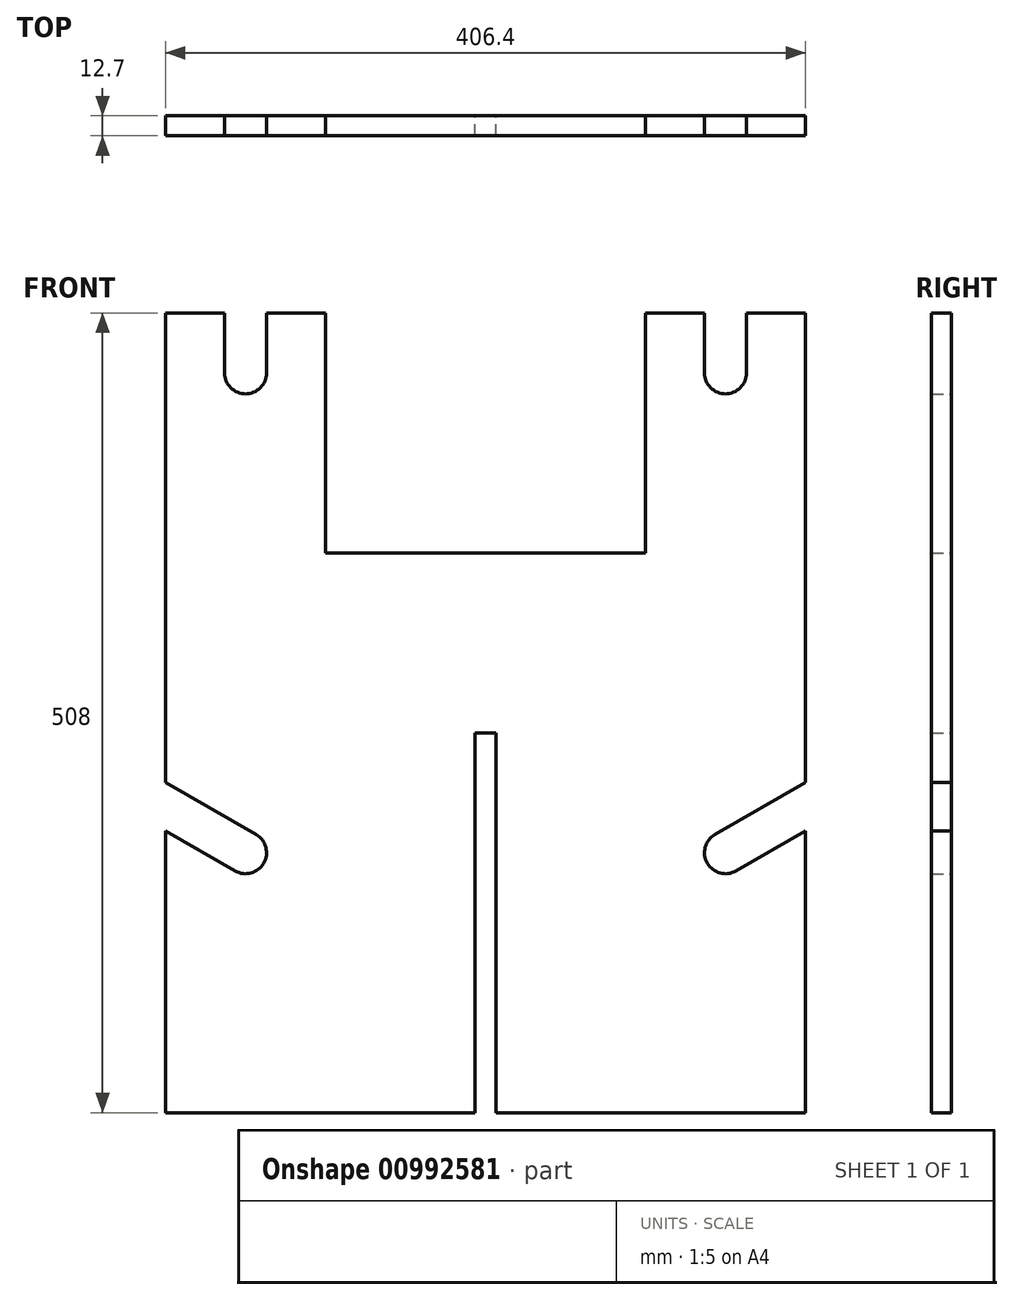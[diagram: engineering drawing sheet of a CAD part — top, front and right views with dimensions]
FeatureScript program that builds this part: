
annotation { "Feature Type Name" : "Feature", "Feature Type Description" : "" }
export const myFeature = defineFeature(function(context is Context, id is Id, definition is map)
    precondition{}
    {
        {
            var Q0;
            Q0=qCreatedBy(makeId("Front.planeOp"),FACE);
            var sketch = newSketch(context, id + "F0", { "sketchPlane" : qUnion([Q0])});
            skLineSegment(sketch, "E0.bottom", {"start": v(-203.2, 254) * mm, "end": v(-165.73, 254) * mm});
            skLineSegment(sketch, "E0.top", {"start": v(-203.2, -254) * mm, "end": v(-184.4, -254) * mm});
            skLineSegment(sketch, "E0.left", {"start": v(-203.2, 254) * mm, "end": v(-203.2, -254) * mm});
            skLineSegment(sketch, "E0.right", {"start": v(203.2, 254) * mm, "end": v(203.2, -254) * mm});
            skPoint(sketch, "E0.middle", {"position": v(0, 0) * mm});
            skPoint(sketch, "E1", {"position": v(-101.6, 254) * mm});
            skLineSegment(sketch, "E2", {"start": v(0, 0) * mm, "end": v(0, 371.22) * mm, "construction": true});
            skLineSegment(sketch, "E3", {"start": v(0, 0) * mm, "end": v(0, -352.5) * mm, "construction": true});
            skLineSegment(sketch, "E4", {"start": v(-249.7, -12.7) * mm, "end": v(258.3, -12.7) * mm, "construction": true});
            skLineSegment(sketch, "E5", {"start": v(-101.6, 254) * mm, "end": v(-101.6, 101.6) * mm});
            skLineSegment(sketch, "E6", {"start": v(-101.6, 101.6) * mm, "end": v(0, 101.6) * mm});
            skPoint(sketch, "E7", {"position": v(-177.8, -12.7) * mm});
            skPoint(sketch, "E8", {"position": v(-184.4, -12.7) * mm});
            skPoint(sketch, "E9.MirrorP", {"position": v(-171.2, -12.7) * mm});
            skLineSegment(sketch, "E10", {"start": v(-184.4, -12.7) * mm, "end": v(-171.2, -12.7) * mm});
            skLineSegment(sketch, "E11.trimOffspring", {"start": v(-171.2, -254) * mm, "end": v(-6.6, -254) * mm});
            skLineSegment(sketch, "E12.MirrorCS", {"start": v(101.6, 254) * mm, "end": v(101.6, 101.6) * mm});
            skLineSegment(sketch, "E13.MirrorCS", {"start": v(101.6, 101.6) * mm, "end": v(0, 101.6) * mm});
            skLineSegment(sketch, "E14.trimOffspring", {"start": v(101.6, 254) * mm, "end": v(203.2, 254) * mm});
            skLineSegment(sketch, "E15", {"start": v(171.2, -12.7) * mm, "end": v(184.4, -12.7) * mm});
            skLineSegment(sketch, "E16.trimOffspring", {"start": v(184.4, -254) * mm, "end": v(203.2, -254) * mm});
            skLineSegment(sketch, "E17", {"start": v(-184.4, -254) * mm, "end": v(-170.47, -254) * mm});
            skLineSegment(sketch, "E18", {"start": v(171.2, -254) * mm, "end": v(188.53, -254) * mm});
            skPoint(sketch, "E19", {"position": v(-6.6, -254) * mm});
            skPoint(sketch, "E20.MirrorP", {"position": v(6.6, -254) * mm});
            skLineSegment(sketch, "E21", {"start": v(-6.6, -254) * mm, "end": v(-6.6, -12.7) * mm});
            skLineSegment(sketch, "E22", {"start": v(-6.6, -12.7) * mm, "end": v(6.6, -12.7) * mm});
            skLineSegment(sketch, "E23", {"start": v(6.6, -12.7) * mm, "end": v(6.6, -254) * mm});
            skLineSegment(sketch, "E24.trimOffspring", {"start": v(6.6, -254) * mm, "end": v(171.2, -254) * mm});
            skPoint(sketch, "E25", {"position": v(-152.4, 254) * mm});
            skPoint(sketch, "E26.MirrorP", {"position": v(152.4, 254) * mm});
            skArc(sketch, "E27", {"start": v(-165.73, 215.9) * mm, "mid": v(-152.4, 202.57) * mm, "end": v(-139.06, 215.9) * mm});
            skLineSegment(sketch, "E28", {"start": v(-165.73, 215.9) * mm, "end": v(-165.73, 254) * mm});
            skLineSegment(sketch, "E29", {"start": v(-139.06, 215.9) * mm, "end": v(-139.06, 254) * mm});
            skLineSegment(sketch, "E30.trimOffspring", {"start": v(-139.06, 254) * mm, "end": v(-101.6, 254) * mm});
            skLineSegment(sketch, "E31.MirrorCS", {"start": v(165.73, 215.9) * mm, "end": v(165.73, 254) * mm});
            skArc(sketch, "E32.MirrorCS", {"start": v(165.73, 215.9) * mm, "mid": v(152.4, 202.57) * mm, "end": v(139.06, 215.9) * mm});
            skLineSegment(sketch, "E33.MirrorCS", {"start": v(139.06, 215.9) * mm, "end": v(139.06, 254) * mm});
            skLineSegment(sketch, "E34", {"start": v(-152.4, 215.9) * mm, "end": v(-152.4, -73.5) * mm, "construction": true});
            skLineSegment(sketch, "E35.MirrorCS", {"start": v(152.4, 215.9) * mm, "end": v(152.4, -73.5) * mm, "construction": true});
            skArc(sketch, "E36", {"start": v(-159.07, -100.45) * mm, "mid": v(-140.85, -95.57) * mm, "end": v(-145.73, -77.35) * mm});
            skArc(sketch, "E37.MirrorC", {"start": v(159.07, -100.45) * mm, "mid": v(140.85, -95.57) * mm, "end": v(145.73, -77.35) * mm});
            skLineSegment(sketch, "E38", {"start": v(-159.07, -100.45) * mm, "end": v(-203.2, -74.97) * mm});
            skLineSegment(sketch, "E39", {"start": v(-145.73, -77.35) * mm, "end": v(-203.2, -44.17) * mm});
            skLineSegment(sketch, "E40.MirrorCS", {"start": v(145.73, -77.35) * mm, "end": v(203.2, -44.17) * mm});
            skLineSegment(sketch, "E41.MirrorCS", {"start": v(159.07, -100.45) * mm, "end": v(203.2, -74.97) * mm});
            skSolve(sketch);
        }
        {
            var Q0;
            Q0=makeQuery(id+"F0.imprint","IMPRINT",FACE,{"disambiguationData":[TD([[makeQuery(id+"F0.imprint","IMPRINT",EDGE,{"derivedFrom":sQuery(id+"F0.wireOp",EDGE,"E0.bottom")}),-1.0]])]});
            extrude(context, id + "F1", {"entities" : qUnion([Q0]), "endBound" : BoundingType.SYMMETRIC, "depth" : 12.7 * mm, "offsetDistance" : 25.4 * mm});
        }
    });
